# Revit family: Atdec-Full_Motion_Mount_Rail-TH-2050-VFM-
name_source: partatom
category: Generic Models
revit_build: Autodesk Revit 2016 (Build: 20150220_1215(x64)
units: mm (PartAtom-declared; Revit-internal decimal feet)

## family parameters
Can host rebar = No
Cut with Voids When Loaded = No
Host = Face
Part Type = Normal
Room Calculation Point = No
Round Connector Dimension = Use Diameter
Shared = No

## types (1)
- TH-2050-VFM
    Assembly Code = E1010800
    Colour Options = Silver
    Default Elevation = 1219 mm
    Description = Full motion wall mount VESA up to 400x400
    Flat Screen maximum supported weight, kg = 35kg (77lb)
    Manufacturer = Atdec
    Master Carton Dimensions = 380mm (15") Length, 380mm (15") Width, 540mm (21.25") Height
    Material = Steel and Aluminium
    Maximum distance from wall (mm) = 540mm (21.26")
    Minimum distance from wall (mm) = 100mm (3.94")
    Model = TH-2050-VFM
    Pan adjustment = 90° at the wall and mounting head
    Product Family = Wall Mount Rail
    Product Information = https://www.atdec.com.au
    Range of movement = Full Motion
    Security feature = Security screw to deter unauthorised removal
    Single Unit Dimensions = 360mm (14.25") Length, 350mm (14") Width, 130mm (5") Height
    Single units per master pack = 4
    Tilt Adjustment = 20° downward and 5° upward tilt
    UPC Code = 881493004733
    URL = www.atdec.com.au
    Universal Height (mm) = From 100 to 400
    Universal Width (mm) = From 100 to 400
    VESA mounting hole pattern, mm = 100x100, 100x200, 200x100, 200x200, 200x300, 200x400, 300x200, 300x300, 400x200, 400x300, 400x400
    Warranty = 10 years
    Weight, master carton = 22.76kg (50.6lb)
    Weight, single unit = 5.48kg (12.2lb)
    Width = 500 mm  [stored 1.64042 ft]

note: [stored X ft] marks values corroborated as IEEE doubles in the binary element streams (Revit-internal decimal feet)

## geometry (parser evidence)
native form markers: Sweep x10
no freeform markers — native parametric forms only
